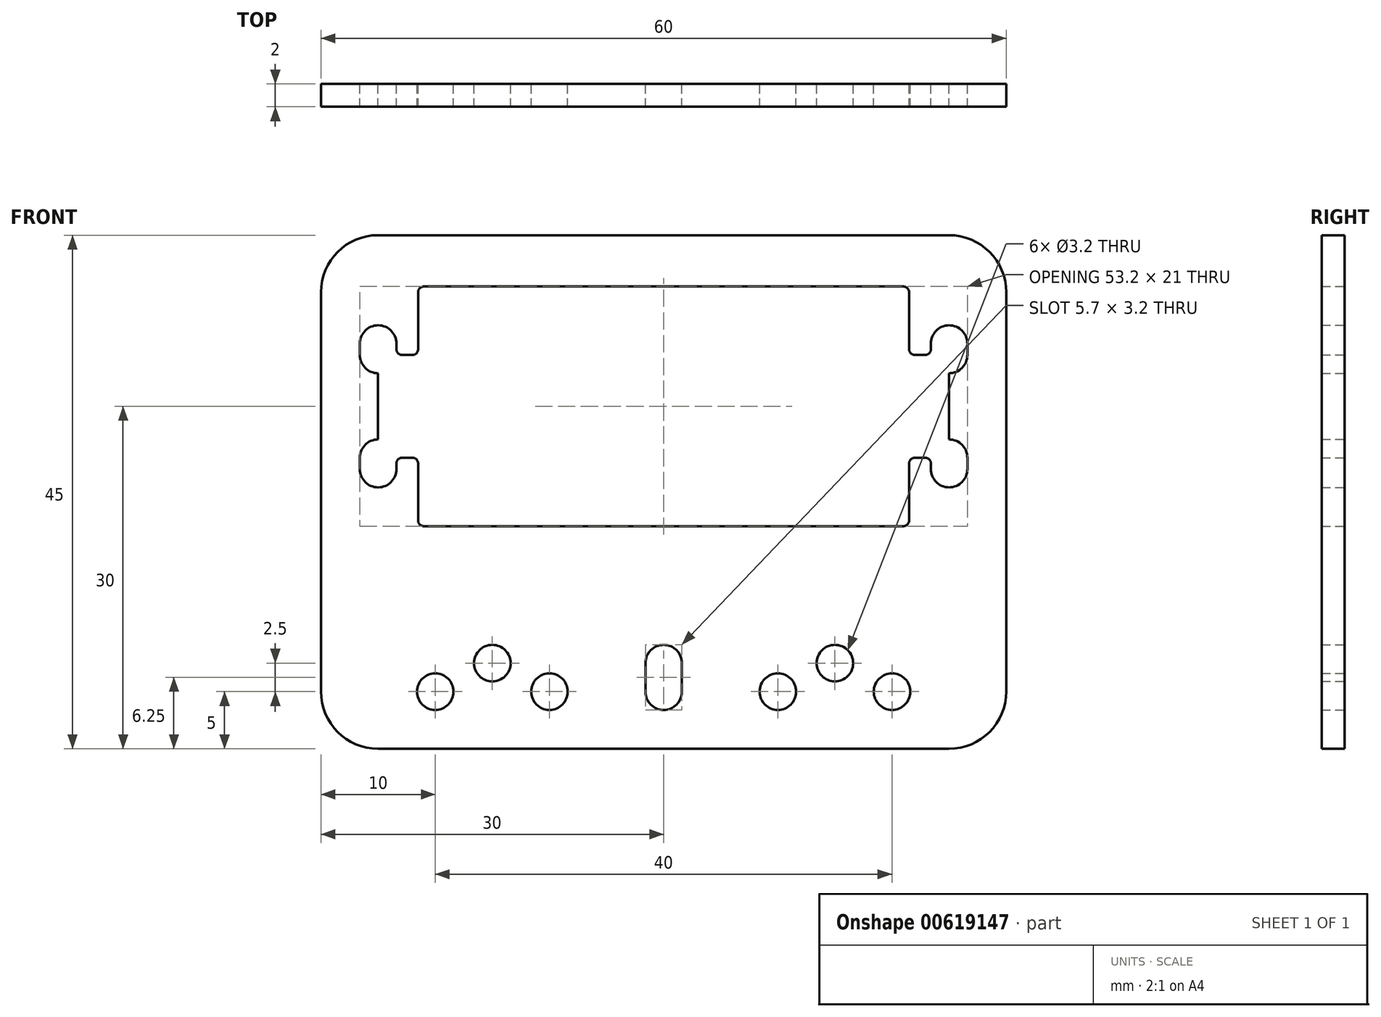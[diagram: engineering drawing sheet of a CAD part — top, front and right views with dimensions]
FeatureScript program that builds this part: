
annotation { "Feature Type Name" : "Feature", "Feature Type Description" : "" }
export const myFeature = defineFeature(function(context is Context, id is Id, definition is map)
    precondition{}
    {
        {
            var Q0;
            Q0=qCreatedBy(makeId("Front.planeOp"),FACE);
            var sketch = newSketch(context, id + "F0", { "sketchPlane" : qUnion([Q0])});
            skLineSegment(sketch, "E0.bottom", {"start": v(5, 0) * mm, "end": v(55, 0) * mm});
            skLineSegment(sketch, "E0.top", {"start": v(5, 45) * mm, "end": v(55, 45) * mm});
            skLineSegment(sketch, "E0.left", {"start": v(0, 5) * mm, "end": v(0, 40) * mm});
            skLineSegment(sketch, "E0.right", {"start": v(60, 5) * mm, "end": v(60, 40) * mm});
            skLineSegment(sketch, "E1", {"start": v(30, 0) * mm, "end": v(30, 45) * mm, "construction": true});
            skLineSegment(sketch, "E2.bottom", {"start": v(51.5, 40.5) * mm, "end": v(8.5, 40.5) * mm, "construction": true});
            skLineSegment(sketch, "E2.top", {"start": v(51.5, 19.5) * mm, "end": v(8.5, 19.5) * mm, "construction": true});
            skLineSegment(sketch, "E2.left", {"start": v(51.5, 40.5) * mm, "end": v(51.5, 19.5) * mm, "construction": true});
            skLineSegment(sketch, "E2.right", {"start": v(8.5, 40.5) * mm, "end": v(8.5, 19.5) * mm, "construction": true});
            skPoint(sketch, "E2.middle", {"position": v(30, 30) * mm});
            skLineSegment(sketch, "E3", {"start": v(8.5, 30) * mm, "end": v(51.5, 30) * mm, "construction": true});
            skPoint(sketch, "E4", {"position": v(5, 35) * mm});
            skPoint(sketch, "E5.MirrorP", {"position": v(55, 35) * mm});
            skPoint(sketch, "E6.MirrorP", {"position": v(5, 25) * mm});
            skPoint(sketch, "E7.MirrorP", {"position": v(55, 25) * mm});
            skArc(sketch, "E8", {"start": v(31.6, 7.5) * mm, "mid": v(30, 9.1) * mm, "end": v(28.4, 7.5) * mm});
            skArc(sketch, "E9", {"start": v(28.4, 5) * mm, "mid": v(30, 3.4) * mm, "end": v(31.6, 5) * mm});
            skLineSegment(sketch, "E10", {"start": v(28.4, 7.5) * mm, "end": v(28.4, 5) * mm});
            skLineSegment(sketch, "E11", {"start": v(31.6, 7.5) * mm, "end": v(31.6, 5) * mm});
            skCircle(sketch, "E12", {"center": v(20, 5) * mm, "radius": 1.6 * mm});
            skCircle(sketch, "E13", {"center": v(15, 7.5) * mm, "radius": 1.6 * mm});
            skCircle(sketch, "E14", {"center": v(10, 5) * mm, "radius": 1.6 * mm});
            skLineSegment(sketch, "E15", {"start": v(10, 5) * mm, "end": v(20, 5) * mm, "construction": true});
            skLineSegment(sketch, "E16", {"start": v(15, 7.5) * mm, "end": v(15, 5) * mm, "construction": true});
            skCircle(sketch, "E17.MirrorC", {"center": v(40, 5) * mm, "radius": 1.6 * mm});
            skCircle(sketch, "E18.MirrorC", {"center": v(45, 7.5) * mm, "radius": 1.6 * mm});
            skCircle(sketch, "E19.MirrorC", {"center": v(50, 5) * mm, "radius": 1.6 * mm});
            skPoint(sketch, "E20.visualSharp", {"position": v(0, 0) * mm});
            skArc(sketch, "E20.filletArc", {"start": v(0, 5) * mm, "mid": v(1.46, 1.46) * mm, "end": v(5, 0) * mm});
            skPoint(sketch, "E21.visualSharp", {"position": v(60, 0) * mm});
            skArc(sketch, "E21.filletArc", {"start": v(55, 0) * mm, "mid": v(58.54, 1.46) * mm, "end": v(60, 5) * mm});
            skPoint(sketch, "E22.visualSharp", {"position": v(60, 45) * mm});
            skArc(sketch, "E22.filletArc", {"start": v(60, 40) * mm, "mid": v(58.54, 43.54) * mm, "end": v(55, 45) * mm});
            skPoint(sketch, "E23.visualSharp", {"position": v(0, 45) * mm});
            skArc(sketch, "E23.filletArc", {"start": v(5, 45) * mm, "mid": v(1.46, 43.54) * mm, "end": v(0, 40) * mm});
            skSolve(sketch);
        }
        {
            var Q0;
            Q0=makeQuery(id+"F0.imprint","IMPRINT",FACE,{"disambiguationData":[TD([[makeQuery(id+"F0.imprint","IMPRINT",EDGE,{"derivedFrom":sQuery(id+"F0.wireOp",EDGE,"E0.bottom")}),1.0]])]});
            extrude(context, id + "F1", {"entities" : qUnion([Q0]), "depth" : 2 * mm, "offsetDistance" : 25 * mm});
        }
        {
            var Q0;
            Q0=qCreatedBy(makeId("Front.planeOp"),FACE);
            var sketch = newSketch(context, id + "F2", { "sketchPlane" : qUnion([Q0])});
            skLineSegment(sketch, "E24", {"start": v(3.4, 35.5) * mm, "end": v(3.4, 34.5) * mm});
            skLineSegment(sketch, "E25", {"start": v(6.6, 35.5) * mm, "end": v(6.6, 35) * mm});
            skLineSegment(sketch, "E26", {"start": v(5, 35.5) * mm, "end": v(5, 34.5) * mm, "construction": true});
            skArc(sketch, "E27", {"start": v(3.4, 34.5) * mm, "mid": v(3.87, 33.37) * mm, "end": v(5, 32.9) * mm});
            skArc(sketch, "E28", {"start": v(6.6, 34.5) * mm, "mid": v(5, 36.1) * mm, "end": v(3.4, 34.5) * mm, "construction": true});
            skArc(sketch, "E29", {"start": v(6.6, 35.5) * mm, "mid": v(5, 37.1) * mm, "end": v(3.4, 35.5) * mm});
            skArc(sketch, "E30", {"start": v(3.4, 35.5) * mm, "mid": v(5, 33.9) * mm, "end": v(6.6, 35.5) * mm, "construction": true});
            skArc(sketch, "E31.MirrorCS", {"start": v(3.4, 25.5) * mm, "mid": v(3.87, 26.63) * mm, "end": v(5, 27.1) * mm});
            skLineSegment(sketch, "E32.MirrorCS", {"start": v(3.4, 24.5) * mm, "end": v(3.4, 25.5) * mm});
            skArc(sketch, "E33.MirrorCS", {"start": v(6.6, 24.5) * mm, "mid": v(5, 22.9) * mm, "end": v(3.4, 24.5) * mm});
            skLineSegment(sketch, "E34.MirrorCS", {"start": v(6.6, 24.5) * mm, "end": v(6.6, 25) * mm});
            skLineSegment(sketch, "E35", {"start": v(5, 32.9) * mm, "end": v(5, 27.1) * mm});
            skLineSegment(sketch, "E36", {"start": v(7.1, 25.5) * mm, "end": v(8, 25.5) * mm});
            skLineSegment(sketch, "E37", {"start": v(7.1, 34.5) * mm, "end": v(8, 34.5) * mm});
            skLineSegment(sketch, "E38.0", {"start": v(8.5, 40) * mm, "end": v(8.5, 35) * mm});
            skLineSegment(sketch, "E39.trimOffspring", {"start": v(8.5, 25) * mm, "end": v(8.5, 20) * mm});
            skPoint(sketch, "E40.visualSharp", {"position": v(6.6, 34.5) * mm});
            skArc(sketch, "E40.filletArc", {"start": v(6.6, 35) * mm, "mid": v(6.75, 34.65) * mm, "end": v(7.1, 34.5) * mm});
            skPoint(sketch, "E41.visualSharp", {"position": v(8.5, 34.5) * mm});
            skArc(sketch, "E41.filletArc", {"start": v(8, 34.5) * mm, "mid": v(8.35, 34.65) * mm, "end": v(8.5, 35) * mm});
            skPoint(sketch, "E42.visualSharp", {"position": v(6.6, 25.5) * mm});
            skArc(sketch, "E42.filletArc", {"start": v(7.1, 25.5) * mm, "mid": v(6.75, 25.35) * mm, "end": v(6.6, 25) * mm});
            skPoint(sketch, "E43.visualSharp", {"position": v(8.5, 25.5) * mm});
            skArc(sketch, "E43.filletArc", {"start": v(8.5, 25) * mm, "mid": v(8.35, 25.35) * mm, "end": v(8, 25.5) * mm});
            skLineSegment(sketch, "E44.MirrorCS", {"start": v(51.5, 40) * mm, "end": v(51.5, 35) * mm});
            skArc(sketch, "E45.MirrorCS", {"start": v(52, 34.5) * mm, "mid": v(51.65, 34.65) * mm, "end": v(51.5, 35) * mm});
            skLineSegment(sketch, "E46.MirrorCS", {"start": v(52.9, 34.5) * mm, "end": v(52, 34.5) * mm});
            skArc(sketch, "E47.MirrorCS", {"start": v(53.4, 35) * mm, "mid": v(53.25, 34.65) * mm, "end": v(52.9, 34.5) * mm});
            skLineSegment(sketch, "E48.MirrorCS", {"start": v(53.4, 35.5) * mm, "end": v(53.4, 35) * mm});
            skArc(sketch, "E49.MirrorCS", {"start": v(53.4, 35.5) * mm, "mid": v(55, 37.1) * mm, "end": v(56.6, 35.5) * mm});
            skLineSegment(sketch, "E50.MirrorCS", {"start": v(56.6, 35.5) * mm, "end": v(56.6, 34.5) * mm});
            skArc(sketch, "E51.MirrorCS", {"start": v(56.6, 34.5) * mm, "mid": v(56.13, 33.37) * mm, "end": v(55, 32.9) * mm});
            skLineSegment(sketch, "E52.MirrorCS", {"start": v(55, 32.9) * mm, "end": v(55, 27.1) * mm});
            skArc(sketch, "E53.MirrorCS", {"start": v(56.6, 25.5) * mm, "mid": v(56.13, 26.63) * mm, "end": v(55, 27.1) * mm});
            skLineSegment(sketch, "E54.MirrorCS", {"start": v(56.6, 24.5) * mm, "end": v(56.6, 25.5) * mm});
            skArc(sketch, "E55.MirrorCS", {"start": v(53.4, 24.5) * mm, "mid": v(55, 22.9) * mm, "end": v(56.6, 24.5) * mm});
            skLineSegment(sketch, "E56.MirrorCS", {"start": v(53.4, 24.5) * mm, "end": v(53.4, 25) * mm});
            skArc(sketch, "E57.MirrorCS", {"start": v(52.9, 25.5) * mm, "mid": v(53.25, 25.35) * mm, "end": v(53.4, 25) * mm});
            skLineSegment(sketch, "E58.MirrorCS", {"start": v(52.9, 25.5) * mm, "end": v(52, 25.5) * mm});
            skArc(sketch, "E59.MirrorCS", {"start": v(51.5, 25) * mm, "mid": v(51.65, 25.35) * mm, "end": v(52, 25.5) * mm});
            skLineSegment(sketch, "E60.MirrorCS", {"start": v(51.5, 25) * mm, "end": v(51.5, 20) * mm});
            skLineSegment(sketch, "E61.0", {"start": v(51, 40.5) * mm, "end": v(9, 40.5) * mm});
            skLineSegment(sketch, "E61.1", {"start": v(51, 19.5) * mm, "end": v(9, 19.5) * mm});
            skPoint(sketch, "E62.visualSharp", {"position": v(8.5, 40.5) * mm});
            skArc(sketch, "E62.filletArc", {"start": v(9, 40.5) * mm, "mid": v(8.65, 40.35) * mm, "end": v(8.5, 40) * mm});
            skPoint(sketch, "E63.visualSharp", {"position": v(51.5, 40.5) * mm});
            skArc(sketch, "E63.filletArc", {"start": v(51.5, 40) * mm, "mid": v(51.35, 40.35) * mm, "end": v(51, 40.5) * mm});
            skPoint(sketch, "E64.visualSharp", {"position": v(51.5, 19.5) * mm});
            skArc(sketch, "E64.filletArc", {"start": v(51, 19.5) * mm, "mid": v(51.35, 19.65) * mm, "end": v(51.5, 20) * mm});
            skPoint(sketch, "E65.visualSharp", {"position": v(8.5, 19.5) * mm});
            skArc(sketch, "E65.filletArc", {"start": v(8.5, 20) * mm, "mid": v(8.65, 19.65) * mm, "end": v(9, 19.5) * mm});
            skSolve(sketch);
        }
        {
            var Q0;
            Q0=makeQuery(id+"F2.imprint","IMPRINT",FACE,{"disambiguationData":[TD([[makeQuery(id+"F2.imprint","IMPRINT",EDGE,{"derivedFrom":sQuery(id+"F2.wireOp",EDGE,"E24")}),1.0]])]});
            extrude(context, id + "F3", {"entities" : qUnion([Q0]), "operationType" : NewBodyOperationType.REMOVE, "endBound" : BoundingType.THROUGH_ALL, "depth" : 25 * mm, "offsetDistance" : 25 * mm});
        }
    });
